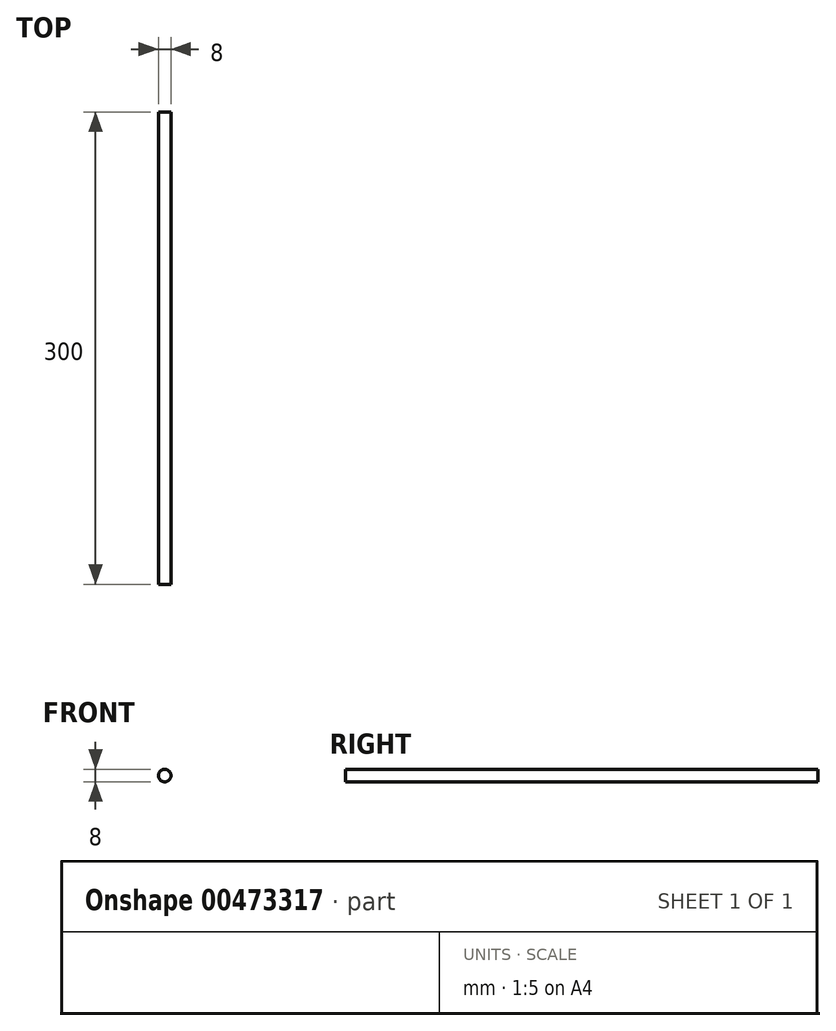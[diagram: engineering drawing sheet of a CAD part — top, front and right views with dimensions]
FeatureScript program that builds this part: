
annotation { "Feature Type Name" : "Feature", "Feature Type Description" : "" }
export const myFeature = defineFeature(function(context is Context, id is Id, definition is map)
    precondition{}
    {
        {
            var Q0;
            Q0=qCreatedBy(makeId("Front.planeOp"),FACE);
            var sketch = newSketch(context, id + "F0", { "sketchPlane" : qUnion([Q0])});
            skCircle(sketch, "E0", {"center": v(0, 0) * mm, "radius": 4 * mm});
            skSolve(sketch);
        }
        {
            var Q0;
            Q0 = qSketchRegion(id + "F0", true);
            extrude(context, id + "F1", {"entities" : qUnion([Q0]), "depth" : 300 * mm});
        }
    });
